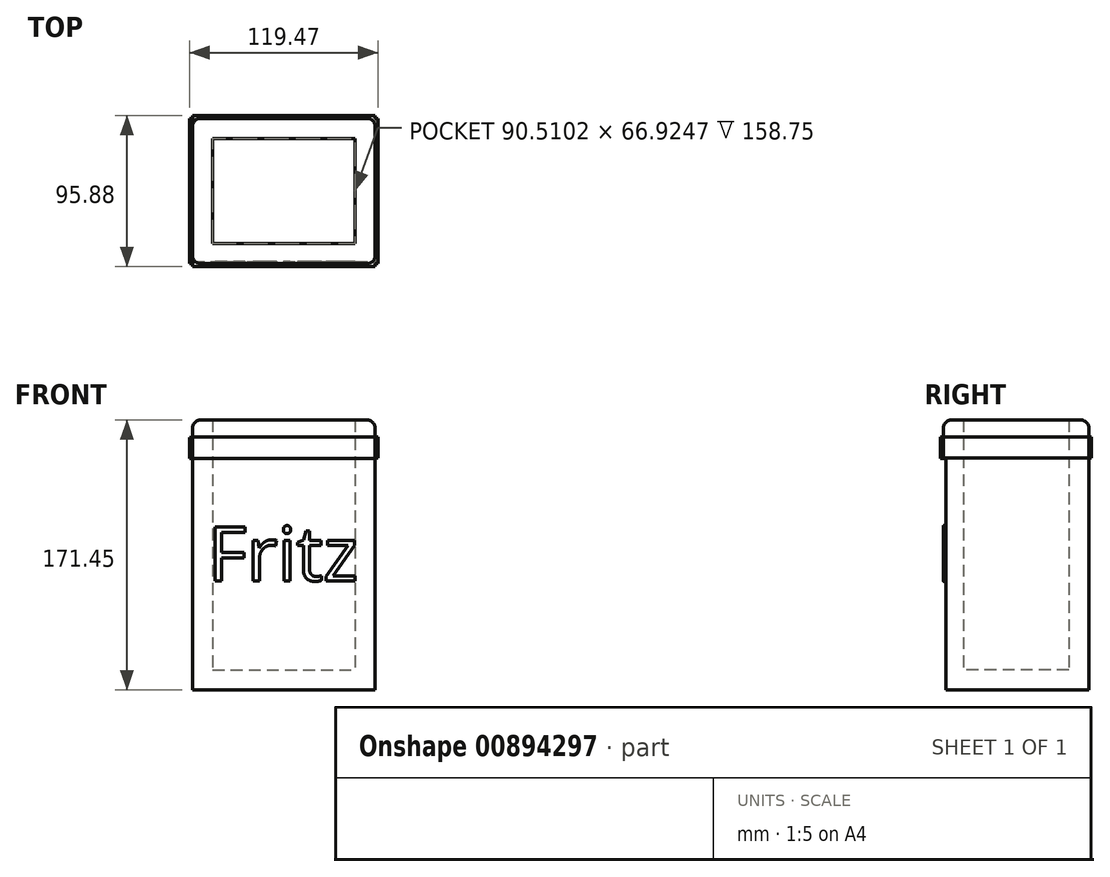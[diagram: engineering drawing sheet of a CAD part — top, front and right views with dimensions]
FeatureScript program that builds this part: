
annotation { "Feature Type Name" : "Feature", "Feature Type Description" : "" }
export const myFeature = defineFeature(function(context is Context, id is Id, definition is map)
    precondition{}
    {
        {
            var Q0;
            Q0=qCreatedBy(makeId("Top.planeOp"),FACE);
            var sketch = newSketch(context, id + "F0", { "sketchPlane" : qUnion([Q0])});
            skLineSegment(sketch, "E0.bottom", {"start": v(-55.62, 24) * mm, "end": v(60.3, 24) * mm});
            skLineSegment(sketch, "E0.top", {"start": v(-55.62, -68.33) * mm, "end": v(60.3, -68.33) * mm});
            skLineSegment(sketch, "E0.left", {"start": v(-55.62, 24) * mm, "end": v(-55.62, -68.33) * mm});
            skLineSegment(sketch, "E0.right", {"start": v(60.3, 24) * mm, "end": v(60.3, -68.33) * mm});
            skSolve(sketch);
        }
        {
            var Q0;
            Q0 = qSketchRegion(id + "F0", true);
            extrude(context, id + "F1", {"entities" : qUnion([Q0]), "depth" : 171.45 * mm, "offsetDistance" : 25.4 * mm});
        }
        {
            var Q0;
            Q0=makeQuery(id+"F1.opExtrude","CAP_FACE",FACE,{"disambiguationData":[OSD([sQuery(id+"F0.wireOp",EDGE,"jIivTuGc-s36s-6Q9N-O8sW-Y5LtDa9iPV9D")])],"isStart":false});
            var Q1;
            Q1=makeQuery(id+"F1.opExtrude","CAP_FACE",FACE,{"disambiguationData":[OSD([sQuery(id+"F0.wireOp",EDGE,"E0.bottom"),sQuery(id+"F0.wireOp",EDGE,"E0.top"),sQuery(id+"F0.wireOp",EDGE,"E0.left"),sQuery(id+"F0.wireOp",EDGE,"E0.right")])],"isStart":false});
            shell(context, id + "F2", {"entities" : qUnion([Q0, Q1]), "thickness" : 12.7 * mm});
        }
        {
            var Q0;
            {var subQ0=sQuery(id+"F0.wireOp",EDGE,"jIivTuGc-s36s-6Q9N-O8sW-Y5LtDa9iPV9D");Q0=makeQuery(id+"F1.opExtrude","CAP_EDGE",EDGE,{"disambiguationData":[OSD([subQ0]),TDD([makeQuery(id+"F0.imprint","IMPRINT",EDGE,{"disambiguationData":[TD([[makeQuery(id+"F0.imprint","INTERSECT",VERTEX,{"derivedFrom":[subQ0,sQuery(id+"F0.wireOp",EDGE,"9WPb5Vre-A5Bn-7tUR-mDDB-g1037OD7vqTw.left")]}),-1.0]])],"derivedFrom":subQ0})])],"isStart":false});}
            var Q1;
            {var subQ0=sQuery(id+"F0.wireOp",EDGE,"jIivTuGc-s36s-6Q9N-O8sW-Y5LtDa9iPV9D");Q1=makeQuery(id+"F1.opExtrude","CAP_EDGE",EDGE,{"disambiguationData":[OSD([subQ0]),TDD([makeQuery(id+"F0.imprint","IMPRINT",EDGE,{"disambiguationData":[TD([[makeQuery(id+"F0.imprint","INTERSECT",VERTEX,{"derivedFrom":[subQ0,sQuery(id+"F0.wireOp",EDGE,"398011f3-cdd4-44c0-aebc-ca6ab49dc7d2.1.2")]}),1.0]])],"derivedFrom":subQ0})])],"isStart":false});}
            var Q2;
            {var subQ0=sQuery(id+"F0.wireOp",EDGE,"jIivTuGc-s36s-6Q9N-O8sW-Y5LtDa9iPV9D");Q2=makeQuery(id+"F1.opExtrude","CAP_EDGE",EDGE,{"disambiguationData":[OSD([subQ0]),TDD([makeQuery(id+"F0.imprint","IMPRINT",EDGE,{"disambiguationData":[TD([[makeQuery(id+"F0.imprint","INTERSECT",VERTEX,{"derivedFrom":[subQ0,sQuery(id+"F0.wireOp",EDGE,"9WPb5Vre-A5Bn-7tUR-mDDB-g1037OD7vqTw.right")]}),1.0]])],"derivedFrom":subQ0})])],"isStart":false});}
            var Q3;
            Q3=makeQuery(id+"F1.opExtrude","CAP_EDGE",EDGE,{"disambiguationData":[OSD([sQuery(id+"F0.wireOp",EDGE,"E0.right")])],"isStart":false});
            var Q4;
            Q4=makeQuery(id+"F1.opExtrude","CAP_EDGE",EDGE,{"disambiguationData":[OSD([sQuery(id+"F0.wireOp",EDGE,"E0.bottom")])],"isStart":false});
            var Q5;
            Q5=makeQuery(id+"F1.opExtrude","CAP_EDGE",EDGE,{"disambiguationData":[OSD([sQuery(id+"F0.wireOp",EDGE,"E0.left")])],"isStart":false});
            var Q6;
            Q6=makeQuery(id+"F1.opExtrude","CAP_EDGE",EDGE,{"disambiguationData":[OSD([sQuery(id+"F0.wireOp",EDGE,"E0.top")])],"isStart":false});
            fillet(context, id + "F3", {"entities" : qUnion([Q0, Q1, Q2, Q3, Q4, Q5, Q6]), "radius" : 5.08 * mm, "tangentPropagation" : true, "allowEdgeOverflow" : false});
        }
        {
            var Q0;
            Q0=makeQuery(id+"F1.opExtrude","SWEPT_FACE",FACE,{"disambiguationData":[OSD([sQuery(id+"F0.wireOp",EDGE,"E0.bottom")])]});
            var sketch = newSketch(context, id + "F4", { "sketchPlane" : qUnion([Q0])});
            skLineSegment(sketch, "E1.bottom", {"start": v(-60.3, 160.6) * mm, "end": v(55.62, 160.6) * mm});
            skLineSegment(sketch, "E1.top", {"start": v(-60.3, 147.35) * mm, "end": v(55.62, 147.35) * mm});
            skLineSegment(sketch, "E1.left", {"start": v(-60.3, 160.6) * mm, "end": v(-60.3, 147.35) * mm});
            skLineSegment(sketch, "E1.right", {"start": v(55.62, 160.6) * mm, "end": v(55.62, 147.35) * mm});
            skSolve(sketch);
        }
        {
            var Q0;
            Q0=makeQuery(id+"F1.opExtrude","SWEPT_FACE",FACE,{"disambiguationData":[OSD([sQuery(id+"F0.wireOp",EDGE,"E0.left")])]});
            var sketch = newSketch(context, id + "F5", { "sketchPlane" : qUnion([Q0])});
            skLineSegment(sketch, "E2.bottom", {"start": v(-24, 160.42) * mm, "end": v(68.33, 160.42) * mm});
            skLineSegment(sketch, "E2.top", {"start": v(-24, 147.17) * mm, "end": v(68.33, 147.17) * mm});
            skLineSegment(sketch, "E2.left", {"start": v(-24, 160.42) * mm, "end": v(-24, 147.17) * mm});
            skLineSegment(sketch, "E2.right", {"start": v(68.33, 160.42) * mm, "end": v(68.33, 147.17) * mm});
            skSolve(sketch);
        }
        {
            var Q0;
            Q0=makeQuery(id+"F4.imprint","IMPRINT",FACE,{"disambiguationData":[TD([[makeQuery(id+"F4.imprint","IMPRINT",EDGE,{"derivedFrom":sQuery(id+"F4.wireOp",EDGE,"E1.bottom")}),-1.0]])]});
            extrude(context, id + "F6", {"entities" : qUnion([Q0]), "operationType" : NewBodyOperationType.ADD, "depth" : 1.78 * mm, "offsetDistance" : 25.4 * mm});
        }
        {
            var Q0;
            Q0=makeQuery(id+"F5.imprint","IMPRINT",FACE,{"disambiguationData":[TD([[makeQuery(id+"F5.imprint","IMPRINT",EDGE,{"derivedFrom":sQuery(id+"F5.wireOp",EDGE,"E2.bottom")}),-1.0]])]});
            extrude(context, id + "F7", {"entities" : qUnion([Q0]), "operationType" : NewBodyOperationType.ADD, "depth" : 1.78 * mm, "offsetDistance" : 25.4 * mm});
        }
        {
            var Q0;
            Q0=makeQuery(id+"F6.boolean.opBoolean","MERGE",FACE,{"derivedFrom":[makeQuery(id+"F1.opExtrude","SWEPT_FACE",FACE,{"disambiguationData":[OSD([sQuery(id+"F0.wireOp",EDGE,"E0.right")])]}),makeQuery(id+"F6.opExtrude","SWEPT_FACE",FACE,{"disambiguationData":[OSD([sQuery(id+"F4.wireOp",EDGE,"E1.left")])]})]});
            var sketch = newSketch(context, id + "F8", { "sketchPlane" : qUnion([Q0])});
            skLineSegment(sketch, "E3.bottom", {"start": v(24, 160.6) * mm, "end": v(-68.33, 160.6) * mm});
            skLineSegment(sketch, "E3.top", {"start": v(24, 147.4) * mm, "end": v(-68.33, 147.4) * mm});
            skLineSegment(sketch, "E3.left", {"start": v(24, 160.6) * mm, "end": v(24, 147.4) * mm});
            skLineSegment(sketch, "E3.right", {"start": v(-68.33, 160.6) * mm, "end": v(-68.33, 147.4) * mm});
            skSolve(sketch);
        }
        {
            var Q0;
            Q0=makeQuery(id+"F8.imprint","IMPRINT",FACE,{"disambiguationData":[TD([[makeQuery(id+"F8.imprint","IMPRINT",EDGE,{"derivedFrom":sQuery(id+"F8.wireOp",EDGE,"E3.bottom")}),1.0]])]});
            extrude(context, id + "F9", {"entities" : qUnion([Q0]), "operationType" : NewBodyOperationType.ADD, "depth" : 1.78 * mm, "offsetDistance" : 25.4 * mm});
        }
        {
            var Q0;
            Q0=makeQuery(id+"F9.boolean.opBoolean","MERGE",FACE,{"derivedFrom":[makeQuery(id+"F7.boolean.opBoolean","MERGE",FACE,{"derivedFrom":[makeQuery(id+"F1.opExtrude","SWEPT_FACE",FACE,{"disambiguationData":[OSD([sQuery(id+"F0.wireOp",EDGE,"E0.top")])]}),makeQuery(id+"F7.opExtrude","SWEPT_FACE",FACE,{"disambiguationData":[OSD([sQuery(id+"F5.wireOp",EDGE,"E2.right")])]})]}),makeQuery(id+"F9.opExtrude","SWEPT_FACE",FACE,{"disambiguationData":[OSD([sQuery(id+"F8.wireOp",EDGE,"E3.right")])]})]});
            var sketch = newSketch(context, id + "F10", { "sketchPlane" : qUnion([Q0])});
            skLineSegment(sketch, "E4.bottom", {"start": v(60.3, 160.6) * mm, "end": v(-55.62, 160.6) * mm});
            skLineSegment(sketch, "E4.top", {"start": v(60.3, 147.17) * mm, "end": v(-55.62, 147.17) * mm});
            skLineSegment(sketch, "E4.left", {"start": v(60.3, 160.6) * mm, "end": v(60.3, 147.17) * mm});
            skLineSegment(sketch, "E4.right", {"start": v(-55.62, 160.6) * mm, "end": v(-55.62, 147.17) * mm});
            skText(sketch, "E5", { "text": "Fritz", "fontName": "OpenSans-Regular.ttf"});
            const initialGuessF10  = {"E5": [-0.0335, 0.08608, 1, 0, 0.02497]};
            skSetInitialGuess(sketch, initialGuessF10);
            skSolve(sketch);
        }
        {
            var Q0;
            {var subQ16=sQuery(id+"F10.wireOp",EDGE,"E4.bottom");Q0=makeQuery(id+"F10.imprint","IMPRINT",FACE,{"disambiguationData":[TD([[makeQuery(id+"F10.imprint","IMPRINT",EDGE,{"derivedFrom":subQ16}),1.0]])]});}
            extrude(context, id + "F11", {"entities" : qUnion([Q0]), "operationType" : NewBodyOperationType.ADD, "depth" : 1.78 * mm, "offsetDistance" : 25.4 * mm});
        }
        {
            var Q0;
            {var subQ0=sQuery(id+"F0.wireOp",EDGE,"E0.left");var subQ1=makeQuery(id+"F9.opExtrude","SWEPT_FACE",FACE,{"disambiguationData":[OSD([sQuery(id+"F8.wireOp",EDGE,"E3.right")])]});var subQ2=sQuery(id+"F0.wireOp",EDGE,"E0.right");var subQ3=sQuery(id+"F0.wireOp",EDGE,"E0.top");var subQ4=makeQuery(id+"F7.opExtrude","SWEPT_FACE",FACE,{"disambiguationData":[OSD([sQuery(id+"F5.wireOp",EDGE,"E2.right")])]});var subQ5=makeQuery(id+"F1.opExtrude","SWEPT_FACE",FACE,{"disambiguationData":[OSD([subQ3])]});Q0=makeQuery(id+"F11.boolean.opBoolean","SPLIT",FACE,{"disambiguationData":[TD([makeQuery(id+"F1.opExtrude","CAP_FACE",FACE,{"disambiguationData":[OSD([sQuery(id+"F0.wireOp",EDGE,"E0.bottom"),subQ3,subQ0,subQ2])],"isStart":true})])],"derivedFrom":makeQuery(id+"F9.boolean.opBoolean","MERGE",FACE,{"derivedFrom":[makeQuery(id+"F7.boolean.opBoolean","MERGE",FACE,{"derivedFrom":[subQ5,subQ4]}),subQ1]})});}
            var sketch = newSketch(context, id + "F12", { "sketchPlane" : qUnion([Q0])});
            skText(sketch, "E6", { "text": "Fritz", "fontName": "OpenSans-Regular.ttf"});
            const initialGuessF12  = {"E6": [-0.0459, 0.06935, 1, 0, 0.0344]};
            skSetInitialGuess(sketch, initialGuessF12);
            skSolve(sketch);
        }
        {
            var Q0;
            Q0=makeQuery(id+"F12.imprint","IMPRINT",FACE,{"disambiguationData":[TD([[makeQuery(id+"F12.imprint","IMPRINT",EDGE,{"derivedFrom":sQuery(id+"F12.wireOp",EDGE,"E6.sketch_text.stroke-0")}),1.0]])]});
            extrude(context, id + "F13", {"entities" : qUnion([Q0]), "operationType" : NewBodyOperationType.REMOVE, "oppositeDirection" : true, "depth" : 1.52 * mm, "offsetDistance" : 25.4 * mm});
        }
        {
            var Q0;
            Q0=makeQuery(id+"F13.boolean.opBoolean","COPY",EDGE,{"derivedFrom":makeQuery(id+"F13.opExtrude","CAP_EDGE",EDGE,{"disambiguationData":[OSD([sQuery(id+"F0.wireOp",EDGE,"E0.top"),sQuery(id+"F0.wireOp",EDGE,"E0.right")])],"isStart":false})});
            var Q1;
            Q1=makeQuery(id+"F13.boolean.opBoolean","COPY",EDGE,{"derivedFrom":makeQuery(id+"F13.opExtrude","CAP_EDGE",EDGE,{"disambiguationData":[OSD([sQuery(id+"F0.wireOp",EDGE,"E0.top"),sQuery(id+"F0.wireOp",EDGE,"E0.left")])],"isStart":false})});
            var Q2;
            {var subQ0=sQuery(id+"F0.wireOp",EDGE,"E0.left");var subQ1=sQuery(id+"F0.wireOp",EDGE,"E0.bottom");Q2=makeQuery(id+"F6.boolean.opBoolean","SPLIT",EDGE,{"disambiguationData":[TD([makeQuery(id+"F6.opExtrude","SWEPT_FACE",FACE,{"disambiguationData":[OSD([sQuery(id+"F4.wireOp",EDGE,"E1.top")])]})])],"derivedFrom":makeQuery(id+"F1.opExtrude","SWEPT_EDGE",EDGE,{"disambiguationData":[OSD([subQ1,subQ0])]})});}
            var Q3;
            {var subQ0=sQuery(id+"F0.wireOp",EDGE,"E0.right");var subQ1=sQuery(id+"F0.wireOp",EDGE,"E0.bottom");Q3=makeQuery(id+"F6.boolean.opBoolean","SPLIT",EDGE,{"disambiguationData":[TD([makeQuery(id+"F6.opExtrude","SWEPT_FACE",FACE,{"disambiguationData":[OSD([sQuery(id+"F4.wireOp",EDGE,"E1.top")])]})])],"derivedFrom":makeQuery(id+"F1.opExtrude","SWEPT_EDGE",EDGE,{"disambiguationData":[OSD([subQ1,subQ0])]})});}
            fillet(context, id + "F14", {"entities" : qUnion([Q0, Q1, Q2, Q3]), "radius" : 5.08 * mm, "tangentPropagation" : true, "allowEdgeOverflow" : false});
        }
        {
            var Q0;
            {var subQ0=sQuery(id+"F0.wireOp",EDGE,"E0.left");var subQ1=sQuery(id+"F0.wireOp",EDGE,"E0.top");Q0=makeQuery(id+"F7.boolean.opBoolean","SPLIT",EDGE,{"disambiguationData":[TD([makeQuery(id+"F3.opFillet","BLEND_FACE",FACE,{"disambiguationData":[OSD([subQ1])]})])],"derivedFrom":makeQuery(id+"F1.opExtrude","SWEPT_EDGE",EDGE,{"disambiguationData":[OSD([subQ1,subQ0])]})});}
            var Q1;
            {var subQ0=sQuery(id+"F0.wireOp",EDGE,"E0.right");var subQ1=sQuery(id+"F0.wireOp",EDGE,"E0.top");Q1=makeQuery(id+"F9.boolean.opBoolean","SPLIT",EDGE,{"disambiguationData":[TD([makeQuery(id+"F3.opFillet","BLEND_FACE",FACE,{"disambiguationData":[OSD([subQ1])]})])],"derivedFrom":makeQuery(id+"F1.opExtrude","SWEPT_EDGE",EDGE,{"disambiguationData":[OSD([subQ1,subQ0])]})});}
            var Q2;
            {var subQ0=sQuery(id+"F0.wireOp",EDGE,"E0.right");var subQ1=sQuery(id+"F0.wireOp",EDGE,"E0.bottom");Q2=makeQuery(id+"F6.boolean.opBoolean","SPLIT",EDGE,{"disambiguationData":[TD([makeQuery(id+"F3.opFillet","BLEND_FACE",FACE,{"disambiguationData":[OSD([subQ1])]})])],"derivedFrom":makeQuery(id+"F1.opExtrude","SWEPT_EDGE",EDGE,{"disambiguationData":[OSD([subQ1,subQ0])]})});}
            var Q3;
            {var subQ0=sQuery(id+"F0.wireOp",EDGE,"E0.bottom");var subQ1=sQuery(id+"F0.wireOp",EDGE,"E0.left");Q3=makeQuery(id+"F6.boolean.opBoolean","SPLIT",EDGE,{"disambiguationData":[TD([makeQuery(id+"F3.opFillet","BLEND_FACE",FACE,{"disambiguationData":[OSD([subQ0])]})])],"derivedFrom":makeQuery(id+"F1.opExtrude","SWEPT_EDGE",EDGE,{"disambiguationData":[OSD([subQ0,subQ1])]})});}
            fillet(context, id + "F15", {"entities" : qUnion([Q0, Q1, Q2, Q3]), "radius" : 5.08 * mm, "tangentPropagation" : true, "allowEdgeOverflow" : false});
        }
    });
